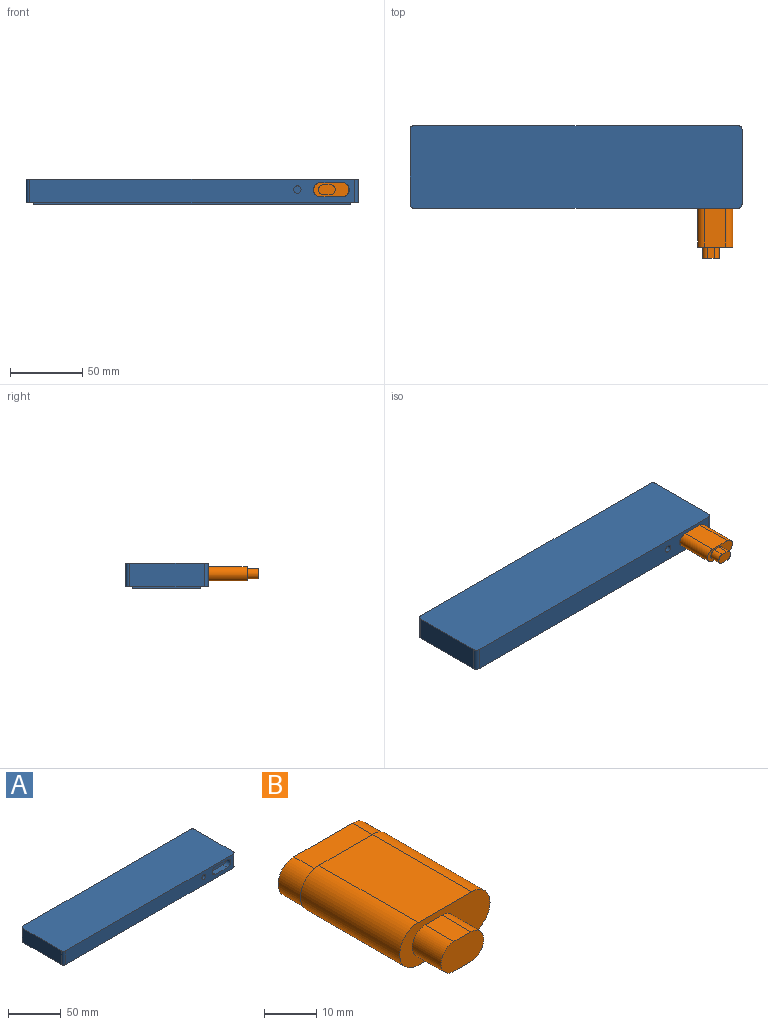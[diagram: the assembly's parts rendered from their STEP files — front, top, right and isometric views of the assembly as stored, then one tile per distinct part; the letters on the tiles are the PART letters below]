
ASSEMBLY  parts=2 mates=1
PART A: 27 faces, bbox 230x57.2x17.7 mm
  f0: plane 224.8x16.15mm, normal (0,1,0), area 3487mm2, adj f4,f5,f12,f13,f22,f23,f24,f25
  f1: plane 224.8x16.15mm, normal (0,-1,0), area 3400.4mm2, adj f4,f5,f11,f14,f15,f16,f17,f18
  f2: plane 51.95x16.15mm, normal (1,0,0), area 839mm2, adj f4,f5,f11,f12
  f3: plane 51.95x16.15mm, normal (-1,0,0), area 839mm2, adj f4,f5,f13,f14
  f4: plane 230x57.15mm, normal (0,0,1), area 13138.7mm2, adj f0,f1,f2,f3,f11,f12,f13,f14
  f5: plane 230x57.15mm, normal (0,0,-1), area 2765.7mm2, adj f0,f1,f2,f3,f6,f7,f8,f9
  f6: plane 220x1.5mm, normal (0,-1,0), area 330mm2, adj f5,f7,f9,f10
  f7: plane 47.15x1.5mm, normal (-1,0,0), area 70.7mm2, adj f5,f6,f8,f10
  f8: plane 220x1.5mm, normal (0,1,0), area 330mm2, adj f5,f7,f9,f10
  f9: plane 47.15x1.5mm, normal (1,0,0), area 70.7mm2, adj f5,f6,f8,f10
  f10: plane 220x47.15mm, normal (0,0,-1), area 10373mm2, adj f6,f7,f8,f9
  f11: cylinder r=2.6mm len=16.15mm, axis (0,0,1), area 66mm2, adj f1,f2,f4,f5
  f12: cylinder r=2.6mm len=16.15mm, axis (0,0,-1), area 66mm2, adj f0,f2,f4,f5
  f13: cylinder r=2.6mm len=16.15mm, axis (0,0,1), area 66mm2, adj f0,f3,f4,f5
  f14: cylinder r=2.6mm len=16.15mm, axis (0,0,-1), area 66mm2, adj f1,f3,f4,f5
  f15: plane 15.9x6mm, normal (0,0,-1), area 95.4mm2, adj f1,f16,f18,f19
  f16: cylinder r=4.55mm len=9.1mm, axis (0,-1,0), area 85.8mm2, adj f1,f15,f17,f19
  f17: plane 15.9x6mm, normal (0,0,1), area 95.4mm2, adj f1,f16,f18,f19
  f18: cylinder r=4.55mm len=9.1mm, axis (0,-1,0), area 85.8mm2, adj f1,f15,f17,f19
  f19: plane 25x9.1mm, normal (0,-1,0), area 209.7mm2, adj f15,f16,f17,f18
  f20: cylinder r=2.55mm len=6mm, axis (0,-1,0), area 96.1mm2, adj f1,f21
  f21: plane 5.1x5.1mm, normal (0,-1,0), area 20.4mm2, adj f20
  f22: plane 19.4x1mm, normal (0,0,1), area 19.4mm2, adj f0,f23,f25,f26
  f23: plane 7.4x1mm, normal (1,0,0), area 7.4mm2, adj f0,f22,f24,f26
  f24: plane 19.4x1mm, normal (0,0,-1), area 19.4mm2, adj f0,f23,f25,f26
  f25: plane 7.4x1mm, normal (-1,0,0), area 7.4mm2, adj f0,f22,f24,f26
  f26: plane 19.4x7.4mm, normal (0,1,0), area 143.6mm2, adj f22,f23,f24,f25
PART B: 17 faces, bbox 24.5x40.8x10 mm
  f0: cylinder r=4.3mm len=8.6mm, axis (0,-1,0), area 82.4mm2, adj f1,f3,f4,f5,f11
  f1: plane 15.9x6.1mm, normal (0,0,-1), area 97mm2, adj f0,f2,f4,f11
  f2: cylinder r=4.3mm len=8.6mm, axis (0,-1,0), area 82.4mm2, adj f1,f3,f4,f5,f11
  f3: plane 15.9x6.1mm, normal (0,0,1), area 97mm2, adj f0,f2,f4,f5
  f4: plane 24.5x8.6mm, normal (0,1,0), area 194.8mm2, adj f0,f1,f2,f3
  f5: plane 24.5x5mm, normal (0,1,0), area 14.4mm2, adj f0,f2,f3,f6,f7,f9
  f6: plane 26.9x14.5mm, normal (0,0,1), area 390mm2, adj f5,f7,f9,f10
  f7: cylinder r=5mm len=26.9mm, axis (0,1,0), area 422.5mm2, adj f5,f6,f8,f10,f11
  f8: plane 26.9x14.5mm, normal (0,0,-1), area 390mm2, adj f7,f9,f10,f11
  f9: cylinder r=5mm len=26.9mm, axis (0,1,0), area 422.5mm2, adj f5,f6,f8,f10,f11
  f10: plane 24.5x10mm, normal (0,-1,0), area 152.9mm2, adj f6,f7,f8,f9,f12,f13,f14,f15
  f11: plane 24.5x5mm, normal (0,1,0), area 14.4mm2, adj f0,f1,f2,f7,f8,f9
  f12: cylinder r=3.5mm len=7.8mm, axis (0,1,0), area 85.8mm2, adj f10,f13,f15,f16
  f13: plane 7.8x4.6mm, normal (0,0,-1), area 35.9mm2, adj f10,f12,f14,f16
  f14: cylinder r=3.5mm len=7.8mm, axis (0,1,0), area 85.8mm2, adj f10,f13,f15,f16
  f15: plane 7.8x4.6mm, normal (0,0,1), area 35.9mm2, adj f10,f12,f14,f16
  f16: plane 11.6x7mm, normal (0,-1,0), area 70.7mm2, adj f12,f13,f14,f15
PLACE A t=(10.7,-69.96,22.43)mm
PLACE B t=(10.7,-70.06,22.43)mm
MATE fastened B.f4 <-> A.f19  axis (0,1,0) through (-7.8,-63.96,31.33)mm
